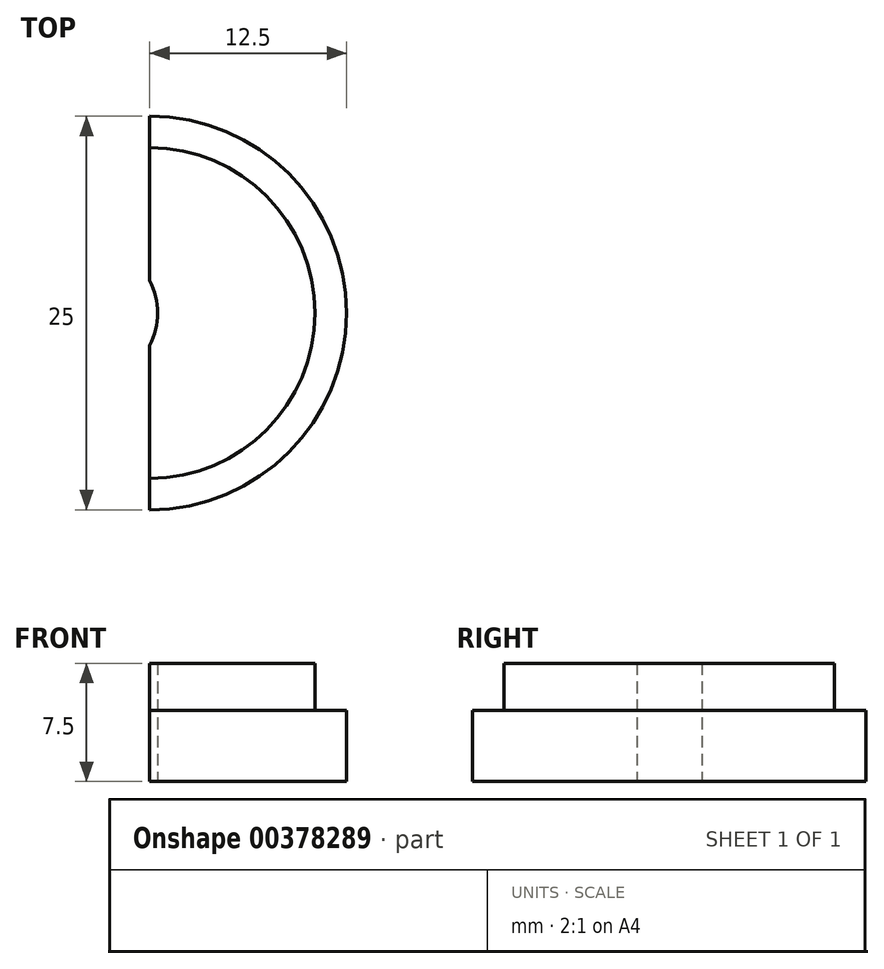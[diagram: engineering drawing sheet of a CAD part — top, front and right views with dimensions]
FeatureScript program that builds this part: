
annotation { "Feature Type Name" : "Feature", "Feature Type Description" : "" }
export const myFeature = defineFeature(function(context is Context, id is Id, definition is map)
    precondition{}
    {
        {
            var Q0;
            Q0=qCreatedBy(makeId("Top.planeOp"),FACE);
            var sketch = newSketch(context, id + "F0", { "sketchPlane" : qUnion([Q0])});
            skCircle(sketch, "E0", {"center": v(0, 0) * mm, "radius": 10.5 * mm});
            skCircle(sketch, "E1", {"center": v(0, 0) * mm, "radius": 12.5 * mm});
            skLineSegment(sketch, "E2", {"start": v(0, 12.5) * mm, "end": v(0, 10.5) * mm});
            skLineSegment(sketch, "E3", {"start": v(0, 10.5) * mm, "end": v(0, -10.5) * mm});
            skLineSegment(sketch, "E4", {"start": v(0, -10.5) * mm, "end": v(0, -12.5) * mm});
            skCircle(sketch, "E5", {"center": v(-4, 0) * mm, "radius": 4.5 * mm});
            skSolve(sketch);
        }
        {
            var Q0;
            {var subQ0=sQuery(id+"F0.wireOp",EDGE,"E3");var subQ4=sQuery(id+"F0.wireOp",EDGE,"E5");var subQ5=makeQuery(id+"F0.imprint","INTERSECT",VERTEX,{"disambiguationData":[OD(0.0)],"derivedFrom":[subQ0,subQ4]});Q0=makeQuery(id+"F0.imprint","IMPRINT",FACE,{"disambiguationData":[TD([[makeQuery(id+"F0.imprint","IMPRINT",EDGE,{"disambiguationData":[TD([[subQ5,1.0]])],"derivedFrom":subQ4}),-1.0]])]});}
            extrude(context, id + "F1", {"entities" : qUnion([Q0]), "depth" : 7.5 * mm});
        }
        {
            var Q0;
            {var subQ1=sQuery(id+"F0.wireOp",EDGE,"E2");Q0=makeQuery(id+"F0.imprint","IMPRINT",FACE,{"disambiguationData":[TD([[makeQuery(id+"F0.imprint","IMPRINT",EDGE,{"derivedFrom":subQ1}),1.0]])]});}
            extrude(context, id + "F2", {"entities" : qUnion([Q0]), "operationType" : NewBodyOperationType.ADD, "depth" : 4.5 * mm});
        }
    });
